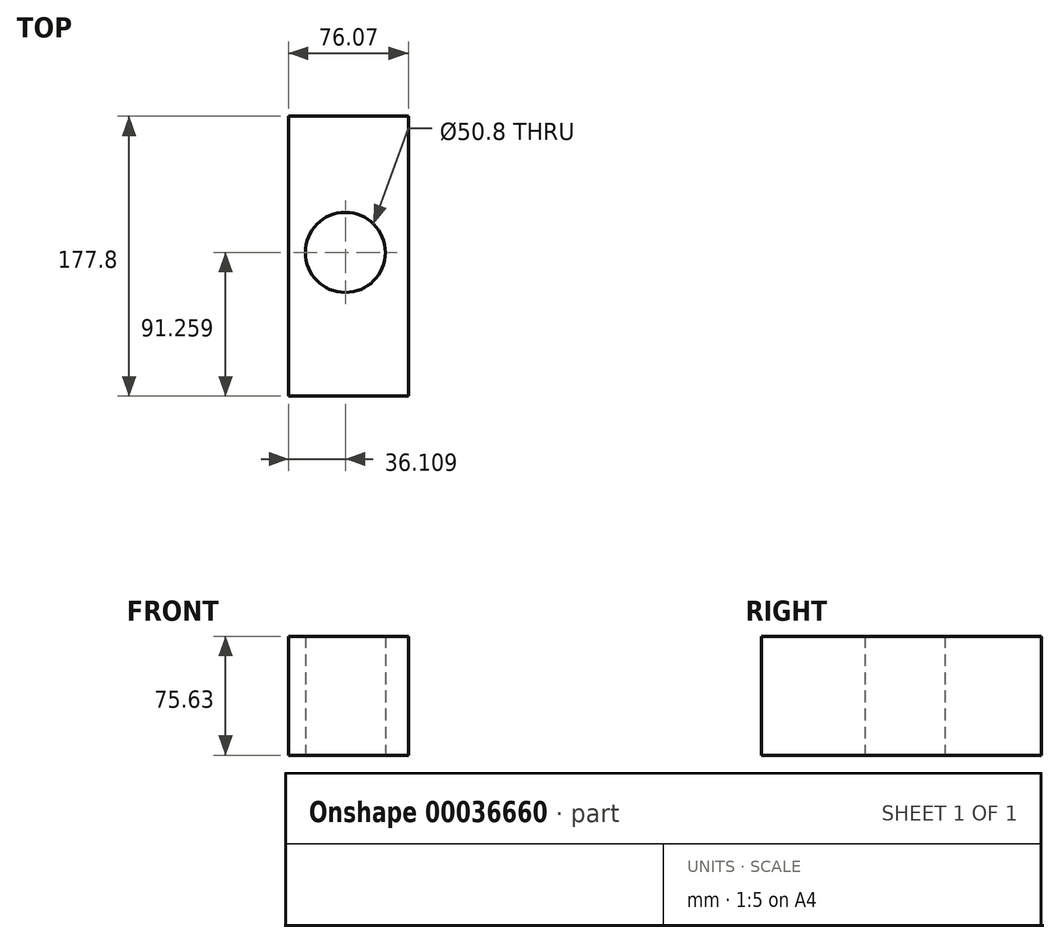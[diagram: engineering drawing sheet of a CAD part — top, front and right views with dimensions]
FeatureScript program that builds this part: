
annotation { "Feature Type Name" : "Feature", "Feature Type Description" : "" }
export const myFeature = defineFeature(function(context is Context, id is Id, definition is map)
    precondition{}
    {
        {
            var Q0;
            Q0=qCreatedBy(makeId("Front.planeOp"),FACE);
            var sketch = newSketch(context, id + "F1", { "sketchPlane" : qUnion([Q0])});
            skLineSegment(sketch, "E0.bottom", {"start": v(0, 0) * mm, "end": v(74.84, 0) * mm});
            skLineSegment(sketch, "E0.top", {"start": v(0, 73.52) * mm, "end": v(74.84, 73.52) * mm});
            skLineSegment(sketch, "E0.left", {"start": v(0, 0) * mm, "end": v(0, 73.52) * mm});
            skLineSegment(sketch, "E0.right", {"start": v(74.84, 0) * mm, "end": v(74.84, 73.52) * mm});
            skLineSegment(sketch, "E1.bottom", {"start": v(0, 0) * mm, "end": v(77.35, 0) * mm});
            skLineSegment(sketch, "E1.top", {"start": v(0, -75.1) * mm, "end": v(77.35, -75.1) * mm});
            skLineSegment(sketch, "E1.left", {"start": v(0, 0) * mm, "end": v(0, -75.1) * mm});
            skLineSegment(sketch, "E1.right", {"start": v(77.35, 0) * mm, "end": v(77.35, -75.1) * mm});
            skLineSegment(sketch, "E2.bottom", {"start": v(0, 0) * mm, "end": v(-76.07, 0) * mm});
            skLineSegment(sketch, "E2.top", {"start": v(0, 75.63) * mm, "end": v(-76.07, 75.63) * mm});
            skLineSegment(sketch, "E2.left", {"start": v(0, 0) * mm, "end": v(0, 75.63) * mm});
            skLineSegment(sketch, "E2.right", {"start": v(-76.07, 0) * mm, "end": v(-76.07, 75.63) * mm});
            skLineSegment(sketch, "E3.bottom", {"start": v(0, -11.6) * mm, "end": v(-76.06, -11.6) * mm});
            skLineSegment(sketch, "E3.top", {"start": v(0, -77.32) * mm, "end": v(-76.06, -77.32) * mm});
            skLineSegment(sketch, "E3.left", {"start": v(0, -11.6) * mm, "end": v(0, -77.32) * mm});
            skLineSegment(sketch, "E3.right", {"start": v(-76.06, -11.6) * mm, "end": v(-76.06, -77.32) * mm});
            skLineSegment(sketch, "E4.bottom", {"start": v(0, -11.6) * mm, "end": v(-76.07, -11.6) * mm});
            skLineSegment(sketch, "E4.left", {"start": v(0, -11.6) * mm, "end": v(0, 0) * mm});
            skLineSegment(sketch, "E4.right", {"start": v(-76.07, -11.6) * mm, "end": v(-76.07, 0) * mm});
            skSolve(sketch);
        }
        {
            var Q0;
            {var subQ2=sQuery(id+"F1.wireOp",EDGE,"E2.top");Q0=makeQuery(id+"F1.imprint","IMPRINT",FACE,{"disambiguationData":[TD([[makeQuery(id+"F1.imprint","IMPRINT",EDGE,{"derivedFrom":subQ2}),1.0]])]});}
            extrude(context, id + "F2", {"entities" : qUnion([Q0]), "depth" : 177.8 * mm});
        }
        {
            var Q0;
            Q0=qCreatedBy(makeId("Top.planeOp"),FACE);
            var sketch = newSketch(context, id + "F3", { "sketchPlane" : qUnion([Q0])});
            skPoint(sketch, "E5", {"position": v(-39.96, -86.54) * mm});
            skSolve(sketch);
        }
        {
            var Q0;
            Q0=sQuery(id+"F3.wireOp",VERTEX,"E5");
            var Q1;
            Q1=makeQuery(id+"F2.opExtrude","SWEPT_BODY",BODY,{"disambiguationData":[OSD([sQuery(id+"F1.wireOp",EDGE,"E2.top"),sQuery(id+"F1.wireOp",EDGE,"E2.left"),sQuery(id+"F1.wireOp",EDGE,"E2.right"),sQuery(id+"F1.wireOp",EDGE,"E2.bottom")])]});
            hole(context, id + "F0", {"style" : HoleStyle.C_SINK, "holeDiameter" : 50.8 * mm, "cSinkDiameter" : 50.8 * mm, "endStyle" : HoleEndStyle.THROUGH, "oppositeDirection" : true, "locations" : qUnion([Q0]), "scope" : qUnion([Q1]), "cSinkAngle" : 90 * degree});
        }
    });
